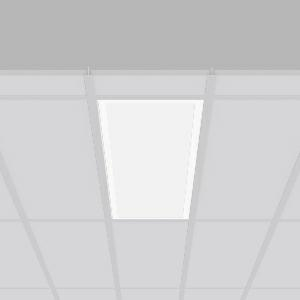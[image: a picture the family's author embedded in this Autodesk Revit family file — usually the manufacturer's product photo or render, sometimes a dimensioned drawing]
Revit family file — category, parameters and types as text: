
# Revit family: sidelite_eco_312367_002_1_790_03ba
name_source: partatom
category: Lighting Fixtures
units: mm (PartAtom-declared; Revit-internal decimal feet)

## family parameters
Cut with Voids When Loaded = No
Host = Face
Light Source = No
Part Type = Normal
Room Calculation Point = No
Round Connector Dimension = Use Diameter
Shared = No

## types (1)
- MultiLumen 1 (1 x LED Modul 840, 3500 lm, 4000)
    Apparent Load = 29 VA
    CIE Flux Codes = 47 79 96 100 100
    Color Rendering = 80
    Color Temperature = 4000
    Default Elevation = 1800 mm
    Description = Series: SIDELITE ECO
Highly economical recessed luminaire with progressive LED technology. Frame made of aluminium, powder-coated. Diffuser: plastic, opal. Lightguide and diffuser made of non-yellowing plastic (PMMA). Lateral light emission (RZB SIDELITE technology) for homogeneous light distribution. External driver. External driver with simple plug-in locking system and extended converter connecting cable to luminaire (1.90 m). MultiLumen: 4 steps adjustable luminous flux. Factory setting is the lowest offered step. Luminaire can be used with accessories (to be ordered separately) as recessed or surface mounting luminaire. Qualified for use in the food and drink industry. 
Colour: white
Length: 1245 mm
Width: 308 mm
Cut-out length: 1233 mm
Cut-out width: 296 mm
Recess height: 160 mm
Luminaire: recess height: 37 mm
Lamp: LED
Socket: without socket
Colour temperature: 4000K
Colour rendering index (CRI): 80
System power: 29 W
Rated luminous flux: 3500 lm
Luminous efficiency: 121 lm/W
System power 2: 33 W
Rated luminous flux 2: 3850 lm
Luminous efficiency 2: 117 lm/W
System power 3: 35 W
Rated luminous flux 3: 4050 lm
Luminous efficiency 3: 116 lm/W
System power 4: 38 W
Rated luminous flux 4: 4400 lm
Luminous efficiency 4: 116 lm/W
Control gear: Regulated power supply
Protection class: II
Type of protection: IP 40
    Height = 0 mm  [stored 0 ft]
    Lamp = 1 x LED Modul 840
    Lamp Light Flux = 3500 lm
    Lamp count = 1
    Length = 1245 mm
    Lifetime = 50000 h
    Luminous efficacy = 121 lm/W
    Manufacturer = RZB
    ModVariant = No
    Model = 312367.002.1.790
    Mounting Place = Ceiling
    Mounting Type = Recessed
    Number of Poles = 1
    OnlyDefault = Yes
    Power Factor = 1
    Product Name = SIDELITE ECO
    Product group = Recessed modular luminaires
    ProductGroupID = 406
    Protection Class = Protection class II
    Protection Degree = IP 20
    RLX_Detail_Level = 1
    RLX_Emergency_Light_Flux = 0 lm
    RLX_Emergency_Type = 0
    RLX_Emergency_Type_DB = No
    RlxData = <blob elided: 31493 chars, md5=627b375e>
    Socket = socket
    Standby Power = 0 W
    System Light Flux = 3500 lm
    System Power = 29 W
    Type Comments = MultiLumen 1
    Type Image = 312367.002.jpg
    URL = http://relux.com
    VarID = multilumen_1
    Voltage = 230 V
    Voltage Range = 220-240 V
    Weight = 0.00 kg
    Width = 308 mm

note: [stored X ft] marks values corroborated as IEEE doubles in the binary element streams (Revit-internal decimal feet)

## geometry (parser evidence)
native form markers: Blend x4, Sweep x10
no freeform markers — native parametric forms only
